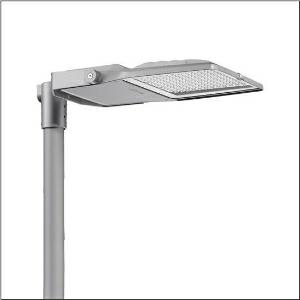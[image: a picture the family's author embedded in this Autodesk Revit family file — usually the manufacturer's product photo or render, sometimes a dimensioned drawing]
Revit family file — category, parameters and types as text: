
# Revit family: floodlight_fl_21_midi___pl43_5xa7786f4a3a_05ab
name_source: partatom
category: Lighting Fixtures
units: mm (PartAtom-declared; Revit-internal decimal feet)

## family parameters
Cut with Voids When Loaded = No
Host = Face
Light Source = No
Part Type = Normal
Room Calculation Point = No
Round Connector Dimension = Use Diameter
Shared = No

## types (1)
- --- (1 x LED, 38290 lm, 271.6 W, 4000K)
    Apparent Load = 272 VA
    CIE Flux Codes = 27 78 99 100 100
    Color Rendering = 70
    Color Temperature = 4000K
    Default Elevation = 1800 mm
    Description = Floodlight FL 21 midi, floodlight, primary light control with lens, of PMMA, primary optical cover: protective disc, of toughened safety glass, transparent, light distribution: PL43, light emission: direct distribution, installation type: surface-mounted, LED, High Power LED, rated luminous flux: 38.290lm, luminous efficacy: 141lm/W, light colour: 740, colour temperature: 4000K, control gear: Smart Interface (Zhaga)D4i, control: overheat protection, constant luminous flux control, time-dependent luminous flux control, flexible luminous flux parameterisation, pre-setting: logarithmic dimming characteristic, with terminal, 6-pole, mains connection: 220..240V, AC, 50/60Hz, start of lifetime: 272W, end of service life: 287W, reduction: 123W, mast bracket, of diecast aluminium, powder-coated, Siteco® metallic grey (DB 702S), corrosivity category C5 mid according to DIN EN ISO 12944, suitable for swimming pools, chlorine-resistant, sealing non-destructively replaceable, mast bracket, of steel, galvanised, powder-coated, Siteco® metallic grey (DB 702S), Smart Interface below and above, protection rating (complete): IP66, insulation class (complete): insulation class II (safety insulation), certification: CE, ENEC, VDE, protection symbol: D, impact resistance: IK08, permissible operating ambient temperature: -40..+40°C, permissible operating ambient temperature for outdoor applications: -40..+50°C, standard: DIN EN 12944, LABS conformity tested according to VDMA 24364:2018-05, packaging unit: 1 piece

Light Distribution: PL43
    Height = 76 mm
    Lamp = 1 x LED
    Lamp Light Flux = 38290 lm
    Lamp Power = 271.6 W
    Lamp count = 1
    Length = 657 mm
    Luminous efficacy = 141 lm/W
    Manufacturer = Siteco
    ModVariant = No
    Model = 5XA7786F4A3A
    Number of Poles = 1
    OnlyDefault = Yes
    Power Factor = 1
    Product Name = Floodlight FL 21 midi | PL43
    Product group = floodlight | pylon annexe
    ProductGroupID = 6200
    Protection Class = Protection class II
    Protection Degree = IP 66
    RLX_Detail_Level = 1
    RLX_Emergency_Light_Flux = 0 lm
    RLX_Emergency_Type = 0
    RLX_Emergency_Type_DB = No
    RlxData = <blob elided: 104393 chars, md5=abca8b18>
    Socket = socket
    Standby Power = 0 W
    System Light Flux = 38290 lm
    System Power = 272 W
    Type Comments = factory setting: luminous flux: 100 % | dim-lin: 254 | 620 mA
    Type Image = l_1007123.jpg
    URL = http://relux.com
    VarID = @adj_089142
    Voltage = 0 V
    Weight = 0.00 kg
    Width = 442 mm

## geometry (parser evidence)
native form markers: Blend x4, Sweep x12
no freeform markers — native parametric forms only
